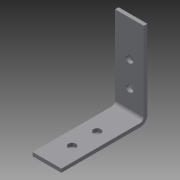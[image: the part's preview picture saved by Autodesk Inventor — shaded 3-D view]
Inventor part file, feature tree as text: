
AUTODESK INVENTOR PART (.ipt)
format: ipt  version: 2013 (Build 170138000, 138)  size: 113,664 bytes
history: native  units: in
note: dims shown in document units (in); Inventor stores cm internally (conversion verified against a paired STEP export)
features: sheet_metal_op x4, sketch x3, other x3
ambient origin geometry x8: Origin, YZ Plane, XZ Plane, XY Plane, X Axis, Y Axis, Z Axis, Center Point
bodies: Solid1 (feature_tree)
feature tree (10):
  sheet_metal_op  "Face1"
  sheet_metal_op  "Flange1"
  sketch  "Sketch1"  dims[d0=3.0in]
  other  "Plate1"
  sketch  "Sketch2"  dims[d1=1.0in]
  other  "Plate2"
  sheet_metal_op  "Bend1"
  sheet_metal_op  "Corner1"
  sketch  "Sketch3"  dims[d3=0.266in d4=0.875in d8=0.266in d10=0.125in d11=0.125in d12=0.0625in d13=0.25in d14=0.125in d15=3.0in d16=90.0deg d17=0.125in d18=0.5in d19=0.125in d20=0.125in d21=0.266in d22=0.266in d23=0.5in d24=0.875in d25=0.875in d26=0.125in d27=0.0in]
  other  "Cut1"
